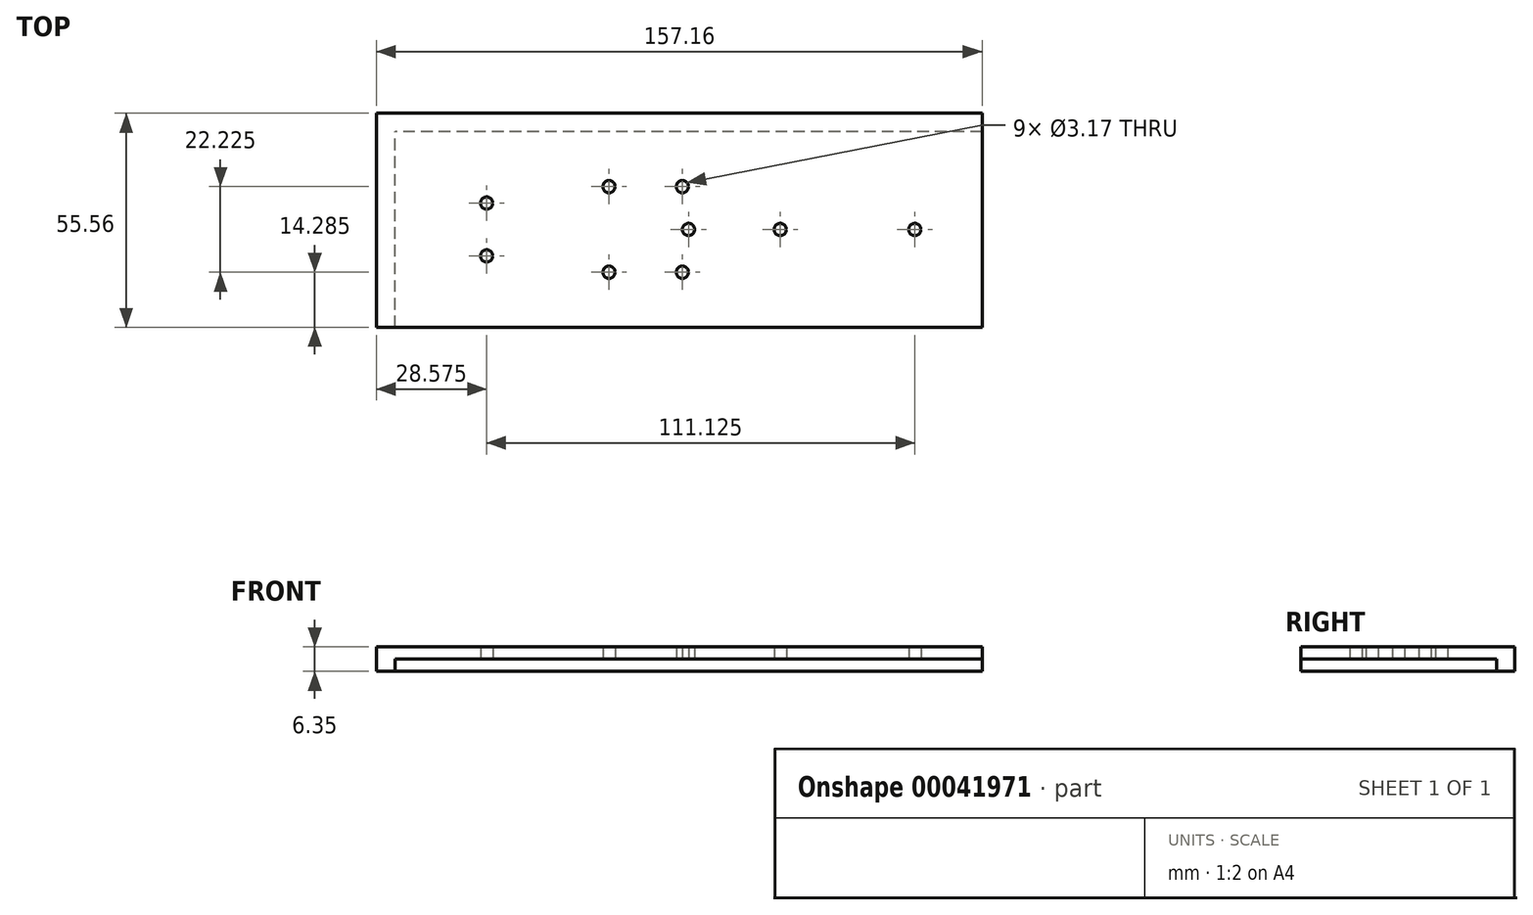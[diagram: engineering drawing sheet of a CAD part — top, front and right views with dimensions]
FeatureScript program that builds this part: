
annotation { "Feature Type Name" : "Feature", "Feature Type Description" : "" }
export const myFeature = defineFeature(function(context is Context, id is Id, definition is map)
    precondition{}
    {
        {
            var Q0;
            Q0=qCreatedBy(makeId("Top.planeOp"),FACE);
            var sketch = newSketch(context, id + "F0", { "sketchPlane" : qUnion([Q0])});
            skLineSegment(sketch, "E0.rect.bottom", {"start": v(76.2, -25.4) * mm, "end": v(-76.2, -25.4) * mm});
            skLineSegment(sketch, "E0.rect.top", {"start": v(76.2, 25.4) * mm, "end": v(-76.2, 25.4) * mm});
            skLineSegment(sketch, "E0.rect.left", {"start": v(76.2, -25.4) * mm, "end": v(76.2, 25.4) * mm});
            skLineSegment(sketch, "E0.rect.right", {"start": v(-76.2, -25.4) * mm, "end": v(-76.2, 25.4) * mm});
            skPoint(sketch, "E0.rect.middle", {"position": v(0, 0) * mm});
            skCircle(sketch, "E1", {"center": v(53.18, 0) * mm, "radius": 16.67 * mm});
            skLineSegment(sketch, "E2.rect.bottom", {"start": v(30.16, -13.5) * mm, "end": v(1.66, -13.5) * mm});
            skLineSegment(sketch, "E2.rect.top", {"start": v(30.16, 13.5) * mm, "end": v(1.66, 13.5) * mm});
            skLineSegment(sketch, "E2.rect.left", {"start": v(30.16, -13.5) * mm, "end": v(30.16, 13.5) * mm});
            skLineSegment(sketch, "E2.rect.right", {"start": v(1.66, -13.5) * mm, "end": v(1.66, 13.5) * mm});
            skPoint(sketch, "E2.rect.middle", {"position": v(15.91, 0) * mm});
            skCircle(sketch, "E3", {"center": v(-28.5, 11.11) * mm, "radius": 4.76 * mm});
            skCircle(sketch, "E4", {"center": v(-9.45, 11.11) * mm, "radius": 4.76 * mm});
            skCircle(sketch, "E5", {"center": v(-28.5, -11.11) * mm, "radius": 4.76 * mm});
            skCircle(sketch, "E6", {"center": v(-9.45, -11.11) * mm, "radius": 4.76 * mm});
            skLineSegment(sketch, "E7.rect.bottom", {"start": v(-40.9, -16.5) * mm, "end": v(-69.85, -16.5) * mm});
            skLineSegment(sketch, "E7.rect.top", {"start": v(-40.9, 16.51) * mm, "end": v(-69.85, 16.51) * mm});
            skLineSegment(sketch, "E7.rect.left", {"start": v(-40.9, -16.5) * mm, "end": v(-40.9, 16.51) * mm});
            skLineSegment(sketch, "E7.rect.right", {"start": v(-69.85, -16.5) * mm, "end": v(-69.85, 16.51) * mm});
            skPoint(sketch, "E7.rect.middle", {"position": v(-55.37, 0) * mm});
            skText(sketch, "E8", { "text": "L", "fontName": "AllertaStencil-Regular.ttf"});
            skText(sketch, "E9", { "text": "R", "fontName": "AllertaStencil-Regular.ttf"});
            skText(sketch, "E10", { "text": "MP3", "fontName": "OpenSans-Bold.ttf"});
            skText(sketch, "E11", { "text": "SUB", "fontName": "AllertaStencil-Regular.ttf"});
            skCircle(sketch, "E12", {"center": v(53.18, 0) * mm, "radius": 9.53 * mm});
            skLineSegment(sketch, "E13.rect.bottom", {"start": v(70.9, -20.1) * mm, "end": v(68.8, -20.1) * mm});
            skLineSegment(sketch, "E13.rect.left", {"start": v(73.43, -17.56) * mm, "end": v(73.43, 3.3) * mm});
            skLineSegment(sketch, "E13.rect.right", {"start": v(66.27, -17.56) * mm, "end": v(66.27, 3.3) * mm});
            skPoint(sketch, "E13.rect.middle", {"position": v(69.85, 0) * mm});
            skPoint(sketch, "E14.visualSharp", {"position": v(66.27, 20.1) * mm});
            skPoint(sketch, "E15.visualSharp", {"position": v(73.43, 20.1) * mm});
            skPoint(sketch, "E16.visualSharp", {"position": v(73.43, -20.1) * mm});
            skArc(sketch, "E16.filletArc", {"start": v(70.9, -20.1) * mm, "mid": v(72.69, -19.35) * mm, "end": v(73.43, -17.56) * mm});
            skPoint(sketch, "E17.visualSharp", {"position": v(66.27, -20.1) * mm});
            skArc(sketch, "E17.filletArc", {"start": v(66.27, -17.56) * mm, "mid": v(67.01, -19.35) * mm, "end": v(68.8, -20.1) * mm});
            skLineSegment(sketch, "E18", {"start": v(68.8, 5.84) * mm, "end": v(70.9, 5.84) * mm});
            skPoint(sketch, "E19.visualSharp", {"position": v(66.27, 5.84) * mm});
            skArc(sketch, "E19.filletArc", {"start": v(68.8, 5.84) * mm, "mid": v(67.01, 5.1) * mm, "end": v(66.27, 3.3) * mm});
            skPoint(sketch, "E20.visualSharp", {"position": v(73.43, 5.84) * mm});
            skArc(sketch, "E20.filletArc", {"start": v(73.43, 3.3) * mm, "mid": v(72.69, 5.1) * mm, "end": v(70.9, 5.84) * mm});
            skText(sketch, "E21", { "text": "THE LISTENER\n", "fontName": "AllertaStencil-Regular.ttf"});
            skPoint(sketch, "E22", {"position": v(-18.98, 0) * mm});
            skCircle(sketch, "E23", {"center": v(15.91, 0) * mm, "radius": 9.53 * mm});
            skLineSegment(sketch, "E24.rect.bottom", {"start": v(76.2, 136.74) * mm, "end": v(-76.2, 136.74) * mm});
            skLineSegment(sketch, "E24.rect.top", {"start": v(76.2, 187.54) * mm, "end": v(-76.2, 187.54) * mm});
            skLineSegment(sketch, "E24.rect.left", {"start": v(76.2, 136.74) * mm, "end": v(76.2, 187.54) * mm});
            skLineSegment(sketch, "E24.rect.right", {"start": v(-76.2, 136.74) * mm, "end": v(-76.2, 187.54) * mm});
            skPoint(sketch, "E24.rect.middle", {"position": v(0, 162.14) * mm});
            skPoint(sketch, "E25", {"position": v(-55.37, 162.14) * mm});
            skPoint(sketch, "E26", {"position": v(-18.98, 162.14) * mm});
            skPoint(sketch, "E27", {"position": v(15.91, 162.14) * mm});
            skPoint(sketch, "E27.positionSnap0", {"position": v(15.91, 13.5) * mm});
            skPoint(sketch, "E28", {"position": v(53.18, 162.14) * mm});
            skCircle(sketch, "E29", {"center": v(53.18, 162.14) * mm, "radius": 9.53 * mm});
            skLineSegment(sketch, "E30.rect.bottom", {"start": v(-40.9, 145.63) * mm, "end": v(-69.85, 145.63) * mm});
            skLineSegment(sketch, "E30.rect.top", {"start": v(-40.9, 178.65) * mm, "end": v(-69.85, 178.65) * mm});
            skLineSegment(sketch, "E30.rect.left", {"start": v(-40.9, 145.63) * mm, "end": v(-40.9, 178.65) * mm});
            skLineSegment(sketch, "E30.rect.right", {"start": v(-69.85, 145.63) * mm, "end": v(-69.85, 178.65) * mm});
            skCircle(sketch, "E31", {"center": v(-9.45, 151.02) * mm, "radius": 4.76 * mm});
            skCircle(sketch, "E32", {"center": v(19.09, 162.14) * mm, "radius": 9.53 * mm});
            skPoint(sketch, "E33.center.orphan", {"position": v(-28.5, 151.02) * mm});
            skPoint(sketch, "E34.center.orphan", {"position": v(-9.45, 173.25) * mm});
            skPoint(sketch, "E35.center.orphan", {"position": v(-25.33, 173.25) * mm});
            skPoint(sketch, "E36.center.orphan", {"position": v(-25.33, 151.02) * mm});
            skLineSegment(sketch, "E37.rect.bottom", {"start": v(76.2, 278.74) * mm, "end": v(-76.2, 278.74) * mm});
            skLineSegment(sketch, "E37.rect.top", {"start": v(76.2, 329.54) * mm, "end": v(-76.2, 329.54) * mm});
            skLineSegment(sketch, "E37.rect.left", {"start": v(76.2, 278.74) * mm, "end": v(76.2, 329.54) * mm});
            skLineSegment(sketch, "E37.rect.right", {"start": v(-76.2, 278.74) * mm, "end": v(-76.2, 329.54) * mm});
            skPoint(sketch, "E37.rect.middle", {"position": v(0, 304.14) * mm});
            skPoint(sketch, "E37.rect.middle.positionSnap0", {"position": v(0, 187.54) * mm});
            skPoint(sketch, "E37.rect.centerSnap0", {"position": v(0, 187.54) * mm});
            skPoint(sketch, "E38.rect.middle", {"position": v(58.72, 304.14) * mm});
            skPoint(sketch, "E39.rect.middle", {"position": v(-55.37, 304.14) * mm});
            skPoint(sketch, "E40", {"position": v(-14.29, 304.14) * mm});
            skPoint(sketch, "E41", {"position": v(-14.29, 293.03) * mm});
            skPoint(sketch, "E42", {"position": v(-14.29, 315.25) * mm});
            skPoint(sketch, "E38.rect.left.start.orphan", {"position": v(72.97, 290.64) * mm});
            skPoint(sketch, "E38.rect.top.start.orphan", {"position": v(72.97, 317.64) * mm});
            skPoint(sketch, "E38.rect.right.end.orphan", {"position": v(44.48, 317.64) * mm});
            skPoint(sketch, "E38.rect.right.start.orphan", {"position": v(44.48, 290.64) * mm});
            skCircle(sketch, "E43", {"center": v(58.72, 304.14) * mm, "radius": 4.76 * mm});
            skCircle(sketch, "E44", {"center": v(23.81, 304.14) * mm, "radius": 4.76 * mm});
            skLineSegment(sketch, "E45.rect.bottom", {"start": v(72.97, 290.64) * mm, "end": v(44.48, 290.64) * mm});
            skLineSegment(sketch, "E45.rect.top", {"start": v(72.97, 317.64) * mm, "end": v(44.48, 317.64) * mm});
            skLineSegment(sketch, "E45.rect.left", {"start": v(72.97, 290.64) * mm, "end": v(72.97, 317.64) * mm});
            skLineSegment(sketch, "E45.rect.right", {"start": v(44.48, 290.64) * mm, "end": v(44.48, 317.64) * mm});
            skCircle(sketch, "E46", {"center": v(58.72, 304.14) * mm, "radius": 9.53 * mm});
            skCircle(sketch, "E47", {"center": v(23.81, 304.14) * mm, "radius": 9.53 * mm});
            skCircle(sketch, "E48", {"center": v(23.81, 304.14) * mm, "radius": 16.68 * mm});
            skPoint(sketch, "E49", {"position": v(-11.11, 304.14) * mm});
            skPoint(sketch, "E50", {"position": v(-1.59, 304.14) * mm});
            skPoint(sketch, "E51.center.orphan", {"position": v(-4.76, 315.25) * mm});
            skCircle(sketch, "E52", {"center": v(-1.59, 315.25) * mm, "radius": 4.76 * mm});
            skPoint(sketch, "E53.center.orphan", {"position": v(-4.76, 293.03) * mm});
            skCircle(sketch, "E54", {"center": v(-1.59, 293.03) * mm, "radius": 4.76 * mm});
            skPoint(sketch, "E55", {"position": v(-20.64, 304.14) * mm});
            skPoint(sketch, "E56.center.orphan", {"position": v(-23.81, 293.03) * mm});
            skCircle(sketch, "E57", {"center": v(-20.64, 293.03) * mm, "radius": 4.76 * mm});
            skPoint(sketch, "E58.center.orphan", {"position": v(-23.81, 315.25) * mm});
            skCircle(sketch, "E59", {"center": v(-20.64, 315.25) * mm, "radius": 4.76 * mm});
            skPoint(sketch, "E60", {"position": v(-52.39, 304.14) * mm});
            skPoint(sketch, "E39.rect.left.end.orphan", {"position": v(-36.83, 322.17) * mm});
            skPoint(sketch, "E61.rect.left.end.orphan", {"position": v(-39.62, 320.52) * mm});
            skPoint(sketch, "E61.rect.bottom.start.orphan", {"position": v(-39.62, 287.75) * mm});
            skPoint(sketch, "E61.rect.right.end.orphan", {"position": v(-71.12, 320.52) * mm});
            skPoint(sketch, "E61.rect.right.start.orphan", {"position": v(-71.12, 287.75) * mm});
            skPoint(sketch, "E39.rect.right.end.orphan", {"position": v(-72.22, 320.52) * mm});
            skPoint(sketch, "E39.rect.bottom.end.orphan", {"position": v(-73.91, 286.1) * mm});
            skPoint(sketch, "E39.rect.bottom.start.orphan", {"position": v(-38.53, 287.75) * mm});
            skLineSegment(sketch, "E62.rect.bottom", {"start": v(-36.64, 287.75) * mm, "end": v(-68.14, 287.75) * mm});
            skLineSegment(sketch, "E62.rect.top", {"start": v(-36.64, 320.52) * mm, "end": v(-68.14, 320.52) * mm});
            skLineSegment(sketch, "E62.rect.left", {"start": v(-36.64, 287.75) * mm, "end": v(-36.64, 320.52) * mm});
            skLineSegment(sketch, "E62.rect.right", {"start": v(-68.14, 287.75) * mm, "end": v(-68.14, 320.52) * mm});
            skLineSegment(sketch, "E63.rect.bottom", {"start": v(-36.82, 287.75) * mm, "end": v(-67.96, 287.75) * mm});
            skLineSegment(sketch, "E63.rect.top", {"start": v(-36.82, 306.8) * mm, "end": v(-67.96, 306.8) * mm});
            skLineSegment(sketch, "E63.rect.left", {"start": v(-36.82, 287.75) * mm, "end": v(-36.82, 306.8) * mm});
            skLineSegment(sketch, "E63.rect.right", {"start": v(-67.96, 287.75) * mm, "end": v(-67.96, 306.8) * mm});
            skPoint(sketch, "E63.rect.middle", {"position": v(-52.39, 297.28) * mm});
            skCircle(sketch, "E64", {"center": v(-52.39, 297.28) * mm, "radius": 1.59 * mm});
            skCircle(sketch, "E65", {"center": v(23.81, 304.14) * mm, "radius": 1.59 * mm});
            skLineSegment(sketch, "E66.rect.bottom", {"start": v(-41.97, 301.47) * mm, "end": v(-62.8, 301.47) * mm});
            skLineSegment(sketch, "E66.rect.top", {"start": v(-41.97, 320.52) * mm, "end": v(-62.8, 320.52) * mm});
            skLineSegment(sketch, "E66.rect.left", {"start": v(-41.97, 301.47) * mm, "end": v(-41.97, 320.52) * mm});
            skLineSegment(sketch, "E66.rect.right", {"start": v(-62.8, 301.47) * mm, "end": v(-62.8, 320.52) * mm});
            skPoint(sketch, "E66.rect.middle", {"position": v(-52.39, 311) * mm});
            skCircle(sketch, "E67", {"center": v(-52.39, 311) * mm, "radius": 1.59 * mm});
            skCircle(sketch, "E68", {"center": v(-52.39, 311) * mm, "radius": 4.76 * mm});
            skCircle(sketch, "E69", {"center": v(-52.39, 297.28) * mm, "radius": 4.76 * mm});
            skLineSegment(sketch, "E70.rect.bottom", {"start": v(331.07, 278.74) * mm, "end": v(178.67, 278.74) * mm});
            skLineSegment(sketch, "E70.rect.top", {"start": v(331.07, 329.54) * mm, "end": v(178.67, 329.54) * mm});
            skLineSegment(sketch, "E70.rect.left", {"start": v(331.07, 278.74) * mm, "end": v(331.07, 329.54) * mm});
            skLineSegment(sketch, "E70.rect.right", {"start": v(178.67, 278.74) * mm, "end": v(178.67, 329.54) * mm});
            skPoint(sketch, "E70.rect.middle", {"position": v(254.87, 304.14) * mm});
            skCircle(sketch, "E71", {"center": v(313.6, 304.14) * mm, "radius": 1.59 * mm});
            skCircle(sketch, "E72", {"center": v(278.68, 304.14) * mm, "radius": 1.59 * mm});
            skPoint(sketch, "E73", {"position": v(243.76, 304.14) * mm});
            skCircle(sketch, "E74", {"center": v(253.28, 293.03) * mm, "radius": 1.59 * mm});
            skCircle(sketch, "E75", {"center": v(253.28, 315.25) * mm, "radius": 1.59 * mm});
            skCircle(sketch, "E76", {"center": v(234.23, 315.25) * mm, "radius": 1.59 * mm});
            skCircle(sketch, "E77", {"center": v(234.23, 293.03) * mm, "radius": 1.59 * mm});
            skCircle(sketch, "E78", {"center": v(202.48, 311) * mm, "radius": 1.59 * mm});
            skCircle(sketch, "E79", {"center": v(202.48, 297.28) * mm, "radius": 1.59 * mm});
            skCircle(sketch, "E80", {"center": v(254.87, 304.14) * mm, "radius": 1.59 * mm});
            skLineSegment(sketch, "E81.rect.top", {"start": v(331.07, 334.3) * mm, "end": v(173.9, 334.3) * mm});
            skLineSegment(sketch, "E81.rect.right", {"start": v(173.9, 278.74) * mm, "end": v(173.9, 334.3) * mm});
            skLineSegment(sketch, "E82", {"start": v(178.67, 278.74) * mm, "end": v(173.9, 278.74) * mm});
            skLineSegment(sketch, "E83", {"start": v(331.07, 329.54) * mm, "end": v(331.07, 334.3) * mm});
            skPoint(sketch, "E81.rect.left.end.orphan", {"position": v(335.83, 334.3) * mm});
            skPoint(sketch, "E81.rect.bottom.start.orphan", {"position": v(335.83, 273.98) * mm});
            skPoint(sketch, "E84.orphan", {"position": v(173.9, 273.98) * mm});
            const initialGuessF0  = {"E8": [-0.0304, 0.01641, 1, 0, 0.00502], "E9": [-0.0304, -0.00471, 1, 0, 0.00471], "E10": [-0.01587, 0.01733, 1, 0, 0.0041], "E11": [-0.01587, -0.00471, 1, 0, 0.00471], "E21": [0, -0.02283, 1, 0, 0.0062]};
            skSetInitialGuess(sketch, initialGuessF0);
            skSolve(sketch);
        }
        {
            var Q0;
            Q0=makeQuery(id+"F0.imprint","IMPRINT",FACE,{"disambiguationData":[TD([[makeQuery(id+"F0.imprint","IMPRINT",EDGE,{"derivedFrom":sQuery(id+"F0.wireOp",EDGE,"E70.rect.bottom")}),-1.0]])]});
            var Q1;
            Q1=makeQuery(id+"F0.imprint","IMPRINT",FACE,{"disambiguationData":[TD([[makeQuery(id+"F0.imprint","IMPRINT",EDGE,{"derivedFrom":sQuery(id+"F0.wireOp",EDGE,"E70.rect.top")}),-1.0]])]});
            extrude(context, id + "F1", {"entities" : qUnion([Q0, Q1]), "depth" : 3.17 * mm});
        }
        {
            var Q0;
            Q0=makeQuery(id+"F0.imprint","IMPRINT",FACE,{"disambiguationData":[TD([[makeQuery(id+"F0.imprint","IMPRINT",EDGE,{"derivedFrom":sQuery(id+"F0.wireOp",EDGE,"E70.rect.top")}),-1.0]])]});
            extrude(context, id + "F2", {"entities" : qUnion([Q0]), "operationType" : NewBodyOperationType.ADD, "oppositeDirection" : true, "depth" : 3.17 * mm});
        }
    });
